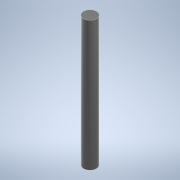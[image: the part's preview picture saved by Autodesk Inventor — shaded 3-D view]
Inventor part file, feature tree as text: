
AUTODESK INVENTOR PART (.ipt)
format: ipt  version: 2022 (Build 260153000, 153)  size: 92,672 bytes
history: native  units: in
note: dims shown in document units (in); Inventor stores cm internally (conversion verified against a paired STEP export)
features: extrude x1, sketch x1
ambient origin geometry x8: Origin, YZ Plane, XZ Plane, XY Plane, X Axis, Y Axis, Z Axis, Center Point
bodies: Solid1 (feature_tree)
feature tree (2):
  extrude  "Extrusion1"  Depth=7.874in TaperAngle=0.0deg
  sketch  "Sketch2"  dims[d0=0.7874in d1=7.874in d2=0.0in]
